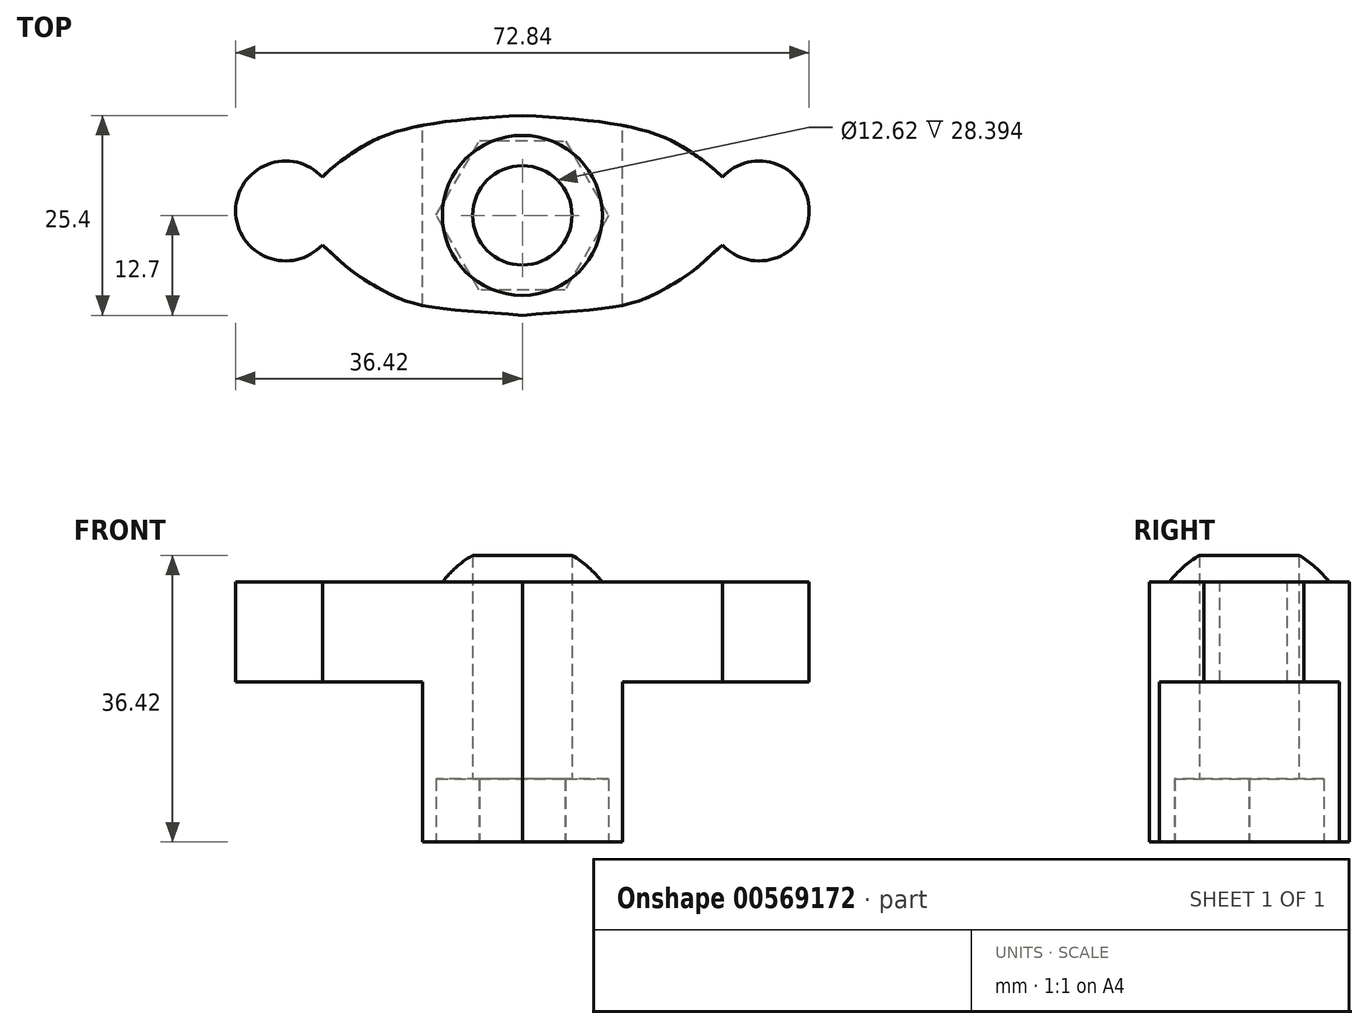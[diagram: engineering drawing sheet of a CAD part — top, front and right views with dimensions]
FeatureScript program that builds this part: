
annotation { "Feature Type Name" : "Feature", "Feature Type Description" : "" }
export const myFeature = defineFeature(function(context is Context, id is Id, definition is map)
    precondition{}
    {
        {
            var Q0;
            Q0=qCreatedBy(makeId("Front.planeOp"),FACE);
            var sketch = newSketch(context, id + "F0", { "sketchPlane" : qUnion([Q0])});
            skLineSegment(sketch, "E0.bottom", {"start": v(0, 0) * mm, "end": v(-25.4, 0) * mm});
            skLineSegment(sketch, "E0.top", {"start": v(0, 25.4) * mm, "end": v(-25.4, 25.4) * mm});
            skLineSegment(sketch, "E0.left", {"start": v(0, 0) * mm, "end": v(0, 25.4) * mm});
            skLineSegment(sketch, "E0.right", {"start": v(-25.4, 0) * mm, "end": v(-25.4, 25.4) * mm});
            skSolve(sketch);
        }
        {
            var Q0;
            Q0=makeQuery(id+"F0.imprint","IMPRINT",FACE,{"disambiguationData":[TD([[makeQuery(id+"F0.imprint","IMPRINT",EDGE,{"derivedFrom":sQuery(id+"F0.wireOp",EDGE,"E0.bottom")}),-1.0]])]});
            extrude(context, id + "F1", {"entities" : qUnion([Q0]), "depth" : 25.4 * mm, "offsetDistance" : 25.4 * mm});
        }
        {
            var Q0;
            Q0=qCreatedBy(makeId("Top.planeOp"),FACE);
            var sketch = newSketch(context, id + "F2", { "sketchPlane" : qUnion([Q0])});
            skCircle(sketch, "E1.cCircle", {"center": v(-12.7, -12.7) * mm, "radius": 9.47 * mm, "construction": true});
            skLineSegment(sketch, "E1.0", {"start": v(-1.76, -12.73) * mm, "end": v(-7.26, -22.2) * mm});
            skLineSegment(sketch, "E1.1", {"start": v(-7.26, -22.2) * mm, "end": v(-18.2, -22.16) * mm});
            skLineSegment(sketch, "E1.2", {"start": v(-18.2, -22.16) * mm, "end": v(-23.64, -12.67) * mm});
            skLineSegment(sketch, "E1.3", {"start": v(-23.64, -12.67) * mm, "end": v(-18.14, -3.2) * mm});
            skLineSegment(sketch, "E1.4", {"start": v(-18.14, -3.2) * mm, "end": v(-7.2, -3.24) * mm});
            skLineSegment(sketch, "E1.5", {"start": v(-7.2, -3.24) * mm, "end": v(-1.76, -12.73) * mm});
            skPoint(sketch, "E1.0.midPoint", {"position": v(-4.5, -17.46) * mm});
            skCircle(sketch, "E2", {"center": v(-12.7, -12.7) * mm, "radius": 6.31 * mm});
            skSolve(sketch);
        }
        {
            var Q0;
            Q0=makeQuery(id+"F2.imprint","IMPRINT",FACE,{"disambiguationData":[TD([[makeQuery(id+"F2.imprint","IMPRINT",EDGE,{"derivedFrom":sQuery(id+"F2.wireOp",EDGE,"E1.0")}),-1.0]])]});
            extrude(context, id + "F3", {"entities" : qUnion([Q0]), "operationType" : NewBodyOperationType.REMOVE, "depth" : 8.03 * mm, "offsetDistance" : 25.4 * mm});
        }
        {
            var Q0;
            Q0=qCreatedBy(makeId("Front.planeOp"),FACE);
            cPlane(context, id + "F4", {"entities" : qUnion([Q0]), "cplaneType" : CPlaneType.OFFSET, "offset" : 12.7 * mm, "width" : 152.4 * mm, "height" : 152.4 * mm});
        }
        {
            var Q0;
            Q0=qCreatedBy(id+"F4.planeOp",FACE);
            var sketch = newSketch(context, id + "F5", { "sketchPlane" : qUnion([Q0])});
            skArc(sketch, "E3", {"start": v(-12.7, 38.1) * mm, "mid": v(-21.68, 34.38) * mm, "end": v(-25.4, 25.4) * mm});
            skLineSegment(sketch, "E4", {"start": v(-12.7, 25.4) * mm, "end": v(-12.7, 38.1) * mm});
            skLineSegment(sketch, "E5", {"start": v(-12.7, 25.4) * mm, "end": v(-25.4, 25.4) * mm});
            skSolve(sketch);
        }
        {
            var Q0;
            Q0=makeQuery(id+"F5.imprint","IMPRINT",FACE,{"disambiguationData":[TD([[makeQuery(id+"F5.imprint","IMPRINT",EDGE,{"derivedFrom":sQuery(id+"F5.wireOp",EDGE,"E3")}),1.0]])]});
            var Q1;
            Q1=sQuery(id+"F5.wireOp",EDGE,"E4");
            revolve(context, id + "F6", {"operationType" : NewBodyOperationType.ADD, "entities" : qUnion([Q0]), "axis" : qUnion([Q1]), "revolveType" : RevolveType.FULL});
        }
        {
            var Q0;
            Q0=qCreatedBy(makeId("Right.planeOp"),FACE);
            var sketch = newSketch(context, id + "F7", { "sketchPlane" : qUnion([Q0])});
            skLineSegment(sketch, "E6.bottom", {"start": v(-25.4, 20.32) * mm, "end": v(0, 20.32) * mm});
            skLineSegment(sketch, "E6.top", {"start": v(-25.4, 33.02) * mm, "end": v(0, 33.02) * mm});
            skLineSegment(sketch, "E6.left", {"start": v(-25.4, 20.32) * mm, "end": v(-25.4, 33.02) * mm});
            skLineSegment(sketch, "E6.right", {"start": v(0, 20.32) * mm, "end": v(0, 33.02) * mm});
            skSolve(sketch);
        }
        {
            var Q0;
            Q0 = qSketchRegion(id + "F7", true);
            extrude(context, id + "F8", {"entities" : qUnion([Q0]), "operationType" : NewBodyOperationType.ADD, "oppositeDirection" : true, "depth" : 50.8 * mm, "offsetDistance" : 25.4 * mm});
        }
        {
            var Q0;
            Q0 = qSketchRegion(id + "F7", true);
            extrude(context, id + "F9", {"entities" : qUnion([Q0]), "operationType" : NewBodyOperationType.ADD, "depth" : 25.4 * mm, "offsetDistance" : 25.4 * mm});
        }
        {
            var Q0;
            {var subQ0=sQuery(id+"F7.wireOp",EDGE,"E6.top");Q0=makeQuery(id+"F9.boolean.opBoolean","MERGE",FACE,{"derivedFrom":[makeQuery(id+"F8.opExtrude","SWEPT_FACE",FACE,{"disambiguationData":[OSD([subQ0])]}),makeQuery(id+"F9.opExtrude","SWEPT_FACE",FACE,{"disambiguationData":[OSD([subQ0])]})]});}
            var sketch = newSketch(context, id + "F10", { "sketchPlane" : qUnion([Q0])});
            skLineSegment(sketch, "E7", {"start": v(-12.7, 0) * mm, "end": v(-38.1, 0) * mm});
            skPoint(sketch, "E8.1.internal.snap0", {"position": v(-25.4, 0) * mm});
            skFitSpline(sketch, "E8", {"points": [v(-12.7, 0) * mm, v(-25.4, -1.27) * mm, v(-31.28, -3.05) * mm, v(-34.54, -4.94) * mm, v(-38.1, -7.83) * mm], "startDerivative": vector(-39.7, -2.17) * mm, "endDerivative": vector(-20.44, -20.31) * mm});
            skLineSegment(sketch, "E9", {"start": v(-38.1, -7.83) * mm, "end": v(-38.1, 0) * mm});
            skLineSegment(sketch, "E10", {"start": v(-12.7, -25.4) * mm, "end": v(-38.1, -25.4) * mm});
            skLineSegment(sketch, "E11", {"start": v(-38.1, -25.4) * mm, "end": v(-38.1, -16.44) * mm});
            skPoint(sketch, "E12.1.internal.snap0", {"position": v(-25.4, -25.4) * mm});
            skFitSpline(sketch, "E12", {"points": [v(-12.7, -25.4) * mm, v(-25.4, -24.13) * mm, v(-30.2, -22.35) * mm, v(-34.35, -19.78) * mm, v(-38.1, -16.44) * mm], "startDerivative": vector(-40.58, 3.65) * mm, "endDerivative": vector(-27.94, 24.86) * mm});
            skCircle(sketch, "E13", {"center": v(-42.77, -12.14) * mm, "radius": 6.35 * mm});
            skLineSegment(sketch, "E14", {"start": v(-12.7, 0) * mm, "end": v(-12.7, -25.4) * mm});
            skFitSpline(sketch, "E15.MirrorCS", {"points": [v(-12.7, -25.4) * mm, v(0, -24.13) * mm, v(4.8, -22.35) * mm, v(8.95, -19.78) * mm, v(12.7, -16.44) * mm], "startDerivative": vector(40.58, 3.65) * mm, "endDerivative": vector(27.94, 24.86) * mm});
            skFitSpline(sketch, "E16.MirrorCS", {"points": [v(-12.7, 0) * mm, v(0, -1.27) * mm, v(5.88, -3.05) * mm, v(9.14, -4.94) * mm, v(12.7, -7.83) * mm], "startDerivative": vector(39.7, -2.17) * mm, "endDerivative": vector(20.44, -20.31) * mm});
            skCircle(sketch, "E17.MirrorC", {"center": v(17.37, -12.14) * mm, "radius": 6.35 * mm});
            skSolve(sketch);
        }
        {
            var Q0;
            Q0=makeQuery(id+"F10.imprint","IMPRINT",FACE,{"disambiguationData":[TD([[makeQuery(id+"F10.imprint","IMPRINT",EDGE,{"derivedFrom":sQuery(id+"F10.wireOp",EDGE,"E7")}),-1.0]])]});
            extrude(context, id + "F11", {"entities" : qUnion([Q0]), "operationType" : NewBodyOperationType.REMOVE, "oppositeDirection" : true, "depth" : 50.8 * mm, "offsetDistance" : 25.4 * mm});
        }
        {
            var Q0;
            Q0=makeQuery(id+"F10.imprint","IMPRINT",FACE,{"disambiguationData":[TD([[makeQuery(id+"F10.imprint","IMPRINT",EDGE,{"derivedFrom":sQuery(id+"F10.wireOp",EDGE,"E10")}),1.0]])]});
            extrude(context, id + "F12", {"entities" : qUnion([Q0]), "operationType" : NewBodyOperationType.REMOVE, "oppositeDirection" : true, "depth" : 50.8 * mm, "offsetDistance" : 25.4 * mm});
        }
        {
            var Q0;
            {var subQ3=sQuery(id+"F10.wireOp",EDGE,"E9");Q0=makeQuery(id+"F10.imprint","IMPRINT",FACE,{"disambiguationData":[TD([[makeQuery(id+"F10.imprint","IMPRINT",EDGE,{"derivedFrom":subQ3}),1.0]])]});}
            extrude(context, id + "F13", {"entities" : qUnion([Q0]), "operationType" : NewBodyOperationType.REMOVE, "oppositeDirection" : true, "depth" : 25.4 * mm, "offsetDistance" : 25.4 * mm});
        }
        {
            var Q0;
            {var subQ1=sQuery(id+"F10.wireOp",EDGE,"E15.MirrorCS");Q0=makeQuery(id+"F10.imprint","IMPRINT",FACE,{"disambiguationData":[TD([[makeQuery(id+"F10.imprint","IMPRINT",EDGE,{"derivedFrom":subQ1}),-1.0]])]});}
            extrude(context, id + "F14", {"entities" : qUnion([Q0]), "operationType" : NewBodyOperationType.REMOVE, "oppositeDirection" : true, "depth" : 50.8 * mm, "offsetDistance" : 25.4 * mm});
        }
        {
            var Q0;
            Q0=makeQuery(id+"F2.imprint","IMPRINT",FACE,{"disambiguationData":[TD([[makeQuery(id+"F2.imprint","IMPRINT",EDGE,{"derivedFrom":sQuery(id+"F2.wireOp",EDGE,"E2")}),1.0]])]});
            extrude(context, id + "F15", {"entities" : qUnion([Q0]), "operationType" : NewBodyOperationType.REMOVE, "depth" : 50.8 * mm, "offsetDistance" : 25.4 * mm});
        }
    });
